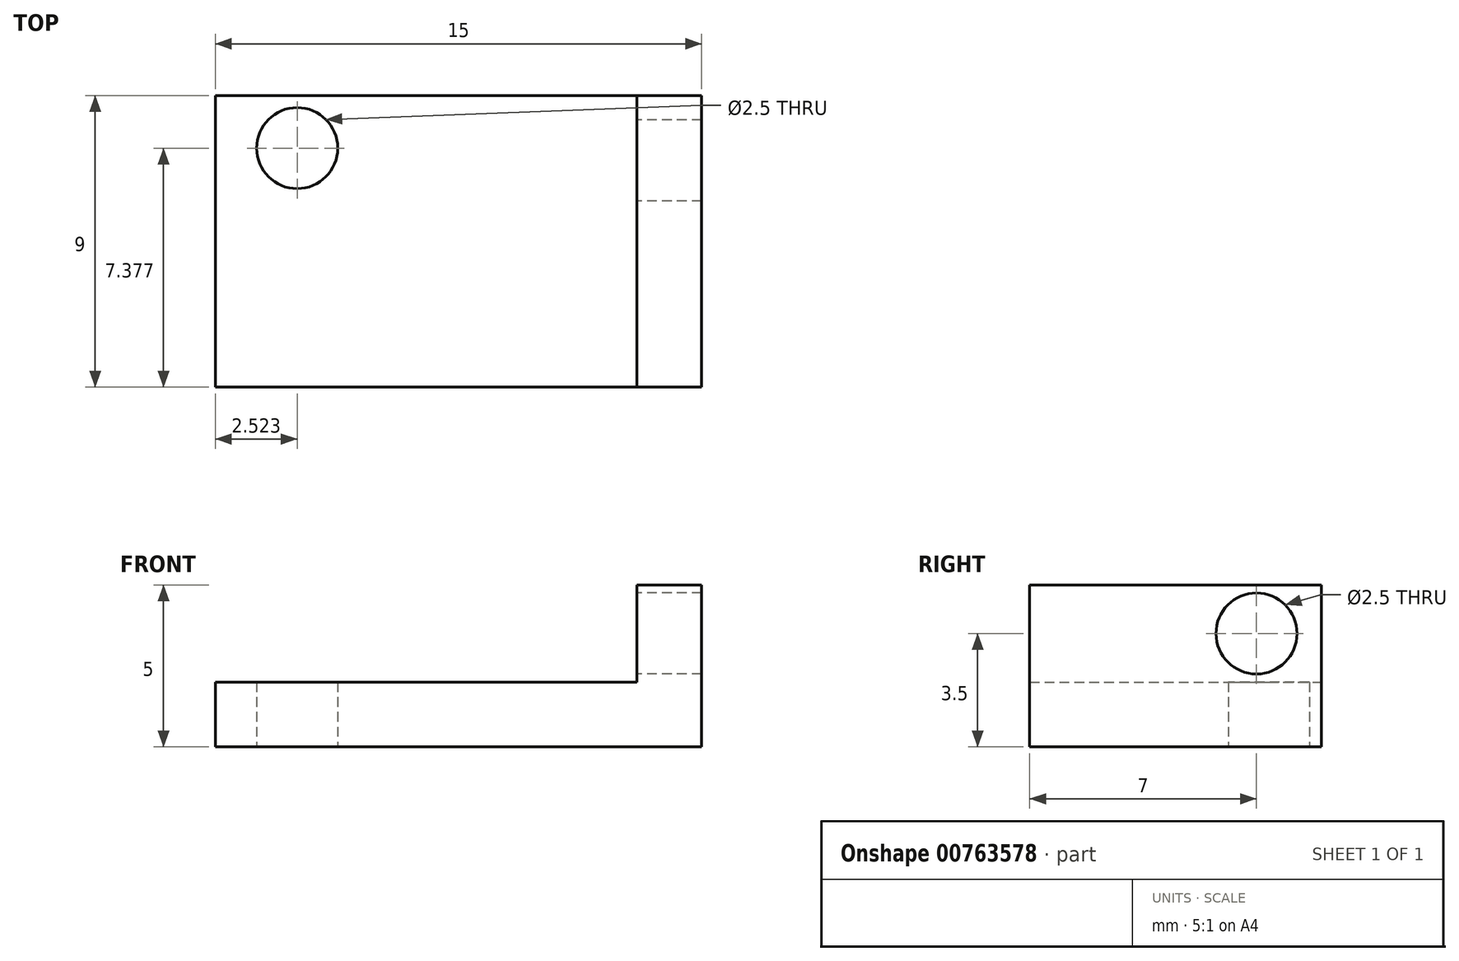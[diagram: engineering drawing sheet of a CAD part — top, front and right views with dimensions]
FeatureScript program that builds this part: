
annotation { "Feature Type Name" : "Feature", "Feature Type Description" : "" }
export const myFeature = defineFeature(function(context is Context, id is Id, definition is map)
    precondition{}
    {
        {
            var Q0;
            Q0=qCreatedBy(makeId("Top.planeOp"),FACE);
            var sketch = newSketch(context, id + "F0", { "sketchPlane" : qUnion([Q0])});
            skLineSegment(sketch, "E0.bottom", {"start": v(0, 0) * mm, "end": v(15, 0) * mm});
            skLineSegment(sketch, "E0.top", {"start": v(0, 9) * mm, "end": v(15, 9) * mm});
            skLineSegment(sketch, "E0.left", {"start": v(0, 0) * mm, "end": v(0, 9) * mm});
            skLineSegment(sketch, "E0.right", {"start": v(15, 0) * mm, "end": v(15, 9) * mm});
            skCircle(sketch, "E1", {"center": v(2.52, 7.38) * mm, "radius": 1.25 * mm});
            skSolve(sketch);
        }
        {
            var Q0;
            Q0=qCreatedBy(makeId("Top.planeOp"),FACE);
            var sketch = newSketch(context, id + "F1", { "sketchPlane" : qUnion([Q0])});
            skPoint(sketch, "E2.0", {"position": v(15, 9) * mm});
            skLineSegment(sketch, "E3.bottom", {"start": v(15, 9) * mm, "end": v(13, 9) * mm});
            skLineSegment(sketch, "E3.top", {"start": v(15, 0) * mm, "end": v(13, 0) * mm});
            skLineSegment(sketch, "E3.left", {"start": v(15, 9) * mm, "end": v(15, 0) * mm});
            skLineSegment(sketch, "E3.right", {"start": v(13, 9) * mm, "end": v(13, 0) * mm});
            skSolve(sketch);
        }
        {
            var Q0;
            Q0=makeQuery(id+"F0.imprint","IMPRINT",FACE,{"disambiguationData":[TD([[makeQuery(id+"F0.imprint","IMPRINT",EDGE,{"derivedFrom":sQuery(id+"F0.wireOp",EDGE,"E0.bottom")}),1.0]])]});
            extrude(context, id + "F2", {"entities" : qUnion([Q0]), "depth" : 2 * mm, "offsetDistance" : 25 * mm});
        }
        {
            var Q0;
            Q0 = qSketchRegion(id + "F1", true);
            extrude(context, id + "F3", {"entities" : qUnion([Q0]), "operationType" : NewBodyOperationType.ADD, "depth" : 5 * mm, "offsetDistance" : 25 * mm});
        }
        {
            var Q0;
            Q0=makeQuery(id+"F3.opExtrude","SWEPT_FACE",FACE,{"disambiguationData":[OSD([sQuery(id+"F1.wireOp",EDGE,"E3.right")])]});
            var sketch = newSketch(context, id + "F4", { "sketchPlane" : qUnion([Q0])});
            skCircle(sketch, "E4", {"center": v(-7, 3.5) * mm, "radius": 1.25 * mm});
            skPoint(sketch, "E4.centerSnap0", {"position": v(-9, 3.5) * mm});
            skSolve(sketch);
        }
        {
            var Q0;
            Q0 = qSketchRegion(id + "F4", true);
            extrude(context, id + "F5", {"entities" : qUnion([Q0]), "operationType" : NewBodyOperationType.REMOVE, "oppositeDirection" : true, "depth" : 25 * mm, "offsetDistance" : 25 * mm});
        }
    });
